# Revit family: P401W
name_source: partatom
category: Generic Models
revit_build: Autodesk Revit Architecture 2012 (Build: 20110309_2315(x64)
units: mm (PartAtom-declared; Revit-internal decimal feet)

## types (1)
- P401W
    * = Lens does not ship with projector
    Accessories - ADP-CV1E = Component video to VGA adapter
    Accessories - AEC00609 = 6 to 9  inch adjustable extension column for use with projector mount
    Accessories - AEC012018 = 12 to 18 inch adjustable extension column for use with projector mount
    Accessories - AEC0203 = 2 to 3 foot adjustable extension column for use with projector mount
    Accessories - AEC0305 = 3 to 5 foot adjustable extension column for use with projector mount
    Accessories - MP300CM = Ceiling mount
    Accessories - NP01MR = IR Receiver enables PJ remote to control PC and MAC functions
    Accessories - NP01UCM = Universal ceiling mount for projectors weighing less than 40 pound
    Accessories - NP02LM1 = 802.11b/g/n wireless LAN adapter
    Accessories - NP03CV = Input panel cover
    Accessories - NP23LP = Replacement lamp
    Accessories - RMT-PJ31 = Replacement remote control
    Accessories - RMT-PJ35 = Replacement Remote Control
    Accessories - SCP200 = Adjustable suspended ceiling plate for use with ceiling mount
    Accessories - SPKR30 = Amplified 30 watt speaker
    Assembly Code = E1020500
    Description = Entry Level Installation Projectors
    Dimensions (WxDxH) = 15.7 x 11.1 x 4.5 in / 398 x 282 x 127 mm
    Done. Electrical-Mechanical-General- Data-Other is next = 0 "
    Environmental - Humidity = 20-80% non-condensing
    Environmental - Operating Temperature = 41deg - 104degF / 5deg - 40degC
    Environmental - Storage = -14deg - 122deg / -10deg - 50degC
    Fan Noise = 36 dB normal / 30 dB eco
    Input Current = 3.9 - 1.7A
    Installation Orientation = Floor/Front, Floor/Rear, Ceiling/Front, Ceiling/Rear
    Manufacturer = NEC Display Solutions
    Model = P401W
    Net Weight = 9 lb / 4.1 kg
    Optical - Contrast Ratio (up to) = 4000 : 1
    Optical - Display Technology = 0.59 in. LCD with MLA
    Optical - Keystone Correction = Manual +/- 30 deg
    Optical - Lamp Life (up to) = 4000 hours normal / 6000 hours eco
    Optical - Lamp Type = 240W AC
    Optical - Lens* F-number, f-number = F=1.7 to 2.0, f=17.4 to 29 mm
    Optical - Lens* Focus = Manual
    Optical - Lens* Shift (vertical) = 0 to 0.6V
    Optical - Lens* Zoom = 1.7
    Optical - Light Output (lumens) = 4000
    Optical - Projection Angle = 0 to 9.8 deg tele / 0 to 16.5 deg wide
    Optical - Projection Distance = 2.3 to 47.8 ft / 0.69 to 14.6m
    Optical - Resolution Maximum = UXGA 1600 x 1200
    Optical - Resolution Native = WXGA 1280 x 800
    Optical - Screen Size (diagonal) = 25 to 300 in., 0.64 to 7.6m
    Optical - Throw Ratio = 1.3 to 2.2
    Power Consumption (Eco Mode off / ECO Mode / Standby / Standby-Power Saving = 325W / 231W / 10W / 0.2W
    Power Requirements = 100 - 240V AC, 50/60Hz
    Regulations = UL60950-1, CSA60950-1, FCC Part15 Class B, ICES-03 Class B, NOM-001-SCFI-1993
    Signal Compatibility/Connectivity - Audio = 16W Speaker
    Signal Compatibility/Connectivity - External Control = RS-232, IR, LAN, DDC/CI, USB, Wireless LAN
    Signal Compatibility/Connectivity - HDMI Signal Compatibility = VGA, SVGA, XGA, WXGA, SXGA, 480p, 576p, 720p, 1080i, 1080p
    Signal Compatibility/Connectivity - Input/Output Terminals Audio 1 = L/R RCA (shared by video sources)
    Signal Compatibility/Connectivity - Input/Output Terminals Audio 2 = 1/8 in. stereo
    Signal Compatibility/Connectivity - Input/Output Terminals Audio 3 = 1/8 in. stereo
    Signal Compatibility/Connectivity - Input/Output Terminals Audio Out = Mini stereo (Variable audio out)
    Signal Compatibility/Connectivity - Input/Output Terminals Monitor Out = Yes
    Signal Compatibility/Connectivity - Input/Output Terminals RGB1 (analog) = 15-pin
    Signal Compatibility/Connectivity - Input/Output Terminals RGB2 (digital) = HDMI w/ HDCP
    Signal Compatibility/Connectivity - Input/Output Terminals RGB3 (digital) = HDMI w/ HDCP
    Signal Compatibility/Connectivity - Input/Output Terminals RGB4 (digital) = USB A Type
    Signal Compatibility/Connectivity - Input/Output Terminals Video 1 = RCA
    Signal Compatibility/Connectivity - Input/Output Terminals Video 2 = S-Video
    Signal Compatibility/Connectivity - Macintosh Compatibility = Yes
    Signal Compatibility/Connectivity - Microphone = 1/8 in. stereo
    Signal Compatibility/Connectivity - PC Signal Compatibility = VGA, SVGA, XGA, SXGA, SXGA+, UXGA
    Signal Compatibility/Connectivity - SD/HD Video Signal Compatibility = 1080i, 1080p, 720p,576p, 576i, 480p, 480i, Y/Cb/Cr component (w/ optional adapter - ADP-CV1E)
    Signal Compatibility/Connectivity - Scan Rate, Horizontal = 15 - 100 kHz
    Signal Compatibility/Connectivity - Scan Rate, Vertical = 50 - 120 Hz
    Signal Compatibility/Connectivity - Supported Video Standards = NTSC, NTSC4.43, PAL, PAL-60, PAL-M, PAL-N, SECAM
    Signal Compatibility/Connectivity - Sync Compatibility = Separate Sync /Composite Sync / Sync on G
    Signal Compatibility/Connectivity - Wireless LAN = Optional
    URL = www.necdisplay.com
    Warranty - ADVEXON2-I = Extends term of InstaCare service program to 3 years
    Warranty - NECEW2-I = Extends term of parts and labor warranty to 4 years

## geometry (parser evidence)
native form markers: Sweep x8
no freeform markers — native parametric forms only
